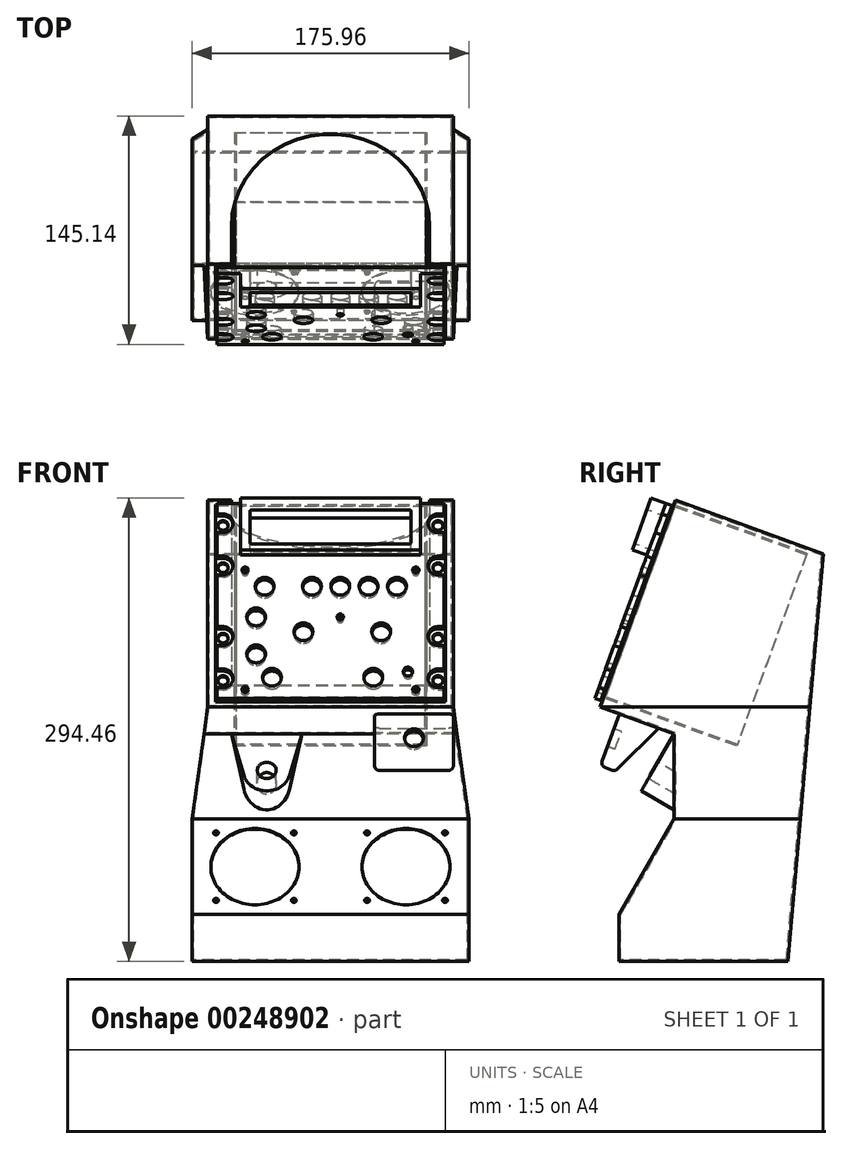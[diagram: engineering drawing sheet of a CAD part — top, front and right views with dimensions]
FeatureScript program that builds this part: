
annotation { "Feature Type Name" : "Feature", "Feature Type Description" : "" }
export const myFeature = defineFeature(function(context is Context, id is Id, definition is map)
    precondition{}
    {
        {
            var Q0;
            Q0=qCreatedBy(makeId("Right.planeOp"),FACE);
            var sketch = newSketch(context, id + "F0", { "sketchPlane" : qUnion([Q0])});
            skLineSegment(sketch, "E0", {"start": v(0, 0) * mm, "end": v(-47.88, -131.56) * mm});
            skLineSegment(sketch, "E1", {"start": v(-47.88, -131.56) * mm, "end": v(-0.9, -148.66) * mm});
            skLineSegment(sketch, "E2", {"start": v(-0.9, -148.66) * mm, "end": v(-0.9, -202.6) * mm});
            skLineSegment(sketch, "E3", {"start": v(-0.9, -202.6) * mm, "end": v(-35.9, -263.21) * mm});
            skLineSegment(sketch, "E4", {"start": v(-35.9, -263.21) * mm, "end": v(-35.9, -293.21) * mm});
            skLineSegment(sketch, "E5", {"start": v(-35.9, -293.21) * mm, "end": v(71.3, -293.21) * mm});
            skLineSegment(sketch, "E6", {"start": v(71.3, -293.21) * mm, "end": v(93.97, -34.2) * mm});
            skLineSegment(sketch, "E7", {"start": v(93.97, -34.2) * mm, "end": v(0, 0) * mm});
            skSolve(sketch);
        }
        {
            var Q0;
            Q0=qSketchRegion(id+"F0",true);
            extrude(context, id + "F1", {"entities" : qUnion([Q0]), "depth" : 200 * mm});
        }
        {
            var Q0;
            Q0=makeQuery(id+"F1.opExtrude","SWEPT_FACE",FACE,{"disambiguationData":[OSD([sQuery(id+"F0.wireOp",EDGE,"E2")])]});
            var sketch = newSketch(context, id + "F2", { "sketchPlane" : qUnion([Q0])});
            skLineSegment(sketch, "E8", {"start": v(178, 0) * mm, "end": v(178, -131.56) * mm});
            skLineSegment(sketch, "E9", {"start": v(178, -131.56) * mm, "end": v(187.98, -202.6) * mm});
            skLineSegment(sketch, "E10", {"start": v(187.98, -202.6) * mm, "end": v(187.98, -293.21) * mm});
            skLineSegment(sketch, "E11", {"start": v(187.98, -293.21) * mm, "end": v(228, -293.21) * mm});
            skLineSegment(sketch, "E12", {"start": v(228, -293.21) * mm, "end": v(228, 0) * mm});
            skLineSegment(sketch, "E13", {"start": v(228, 0) * mm, "end": v(178, 0) * mm});
            skLineSegment(sketch, "E14", {"start": v(0, 0) * mm, "end": v(22, 0) * mm});
            skLineSegment(sketch, "E15", {"start": v(22, 0) * mm, "end": v(22, -131.56) * mm});
            skLineSegment(sketch, "E16", {"start": v(22, -131.56) * mm, "end": v(12.02, -202.6) * mm});
            skLineSegment(sketch, "E17", {"start": v(12.02, -202.6) * mm, "end": v(12.02, -293.21) * mm});
            skLineSegment(sketch, "E18", {"start": v(12.02, -293.21) * mm, "end": v(-28, -293.21) * mm});
            skLineSegment(sketch, "E19", {"start": v(-28, -293.21) * mm, "end": v(-28, 0) * mm});
            skLineSegment(sketch, "E20", {"start": v(-28, 0) * mm, "end": v(22, 0) * mm});
            skLineSegment(sketch, "E21", {"start": v(22, -35.34) * mm, "end": v(0, -35.34) * mm, "construction": true});
            skLineSegment(sketch, "E22", {"start": v(178, -36.32) * mm, "end": v(200, -36.32) * mm, "construction": true});
            skSolve(sketch);
        }
        {
            var Q0;
            Q0=qSketchRegion(id+"F2",true);
            var Q1;
            Q1=makeQuery(id+"F1.opExtrude","SWEPT_FACE",FACE,{"disambiguationData":[OSD([sQuery(id+"F0.wireOp",EDGE,"E6")])]});
            extrude(context, id + "F3", {"entities" : qUnion([Q0]), "operationType" : NewBodyOperationType.REMOVE, "endBound" : BoundingType.UP_TO_SURFACE, "oppositeDirection" : true, "endBoundEntityFace" : qUnion([Q1]), "depth" : 25 * mm, "hasSecondDirection" : true, "secondDirectionOppositeDirection" : false, "secondDirectionDepth" : 150 * mm});
        }
        {
            var Q0;
            Q0=makeQuery(id+"F1.opExtrude","SWEPT_FACE",FACE,{"disambiguationData":[OSD([sQuery(id+"F0.wireOp",EDGE,"E0")])]});
            var sketch = newSketch(context, id + "F4", { "sketchPlane" : qUnion([Q0])});
            skLineSegment(sketch, "E23.bottom", {"start": v(37, -1) * mm, "end": v(163, -1) * mm});
            skLineSegment(sketch, "E23.top", {"start": v(37, -125) * mm, "end": v(163, -125) * mm});
            skLineSegment(sketch, "E23.left", {"start": v(37, -1) * mm, "end": v(37, -125) * mm});
            skLineSegment(sketch, "E23.right", {"start": v(163, -1) * mm, "end": v(163, -125) * mm});
            skSolve(sketch);
        }
        {
            var Q0;
            Q0=qSketchRegion(id+"F4",true);
            extrude(context, id + "F5", {"entities" : qUnion([Q0]), "operationType" : NewBodyOperationType.REMOVE, "oppositeDirection" : true, "depth" : 1 * mm});
        }
        {
            var Q0;
            Q0=makeQuery(id+"F5.boolean.opBoolean","COPY",FACE,{"derivedFrom":makeQuery(id+"F5.opExtrude","CAP_FACE",FACE,{"disambiguationData":[OSD([sQuery(id+"F4.wireOp",EDGE,"E23.bottom"),sQuery(id+"F4.wireOp",EDGE,"E23.top"),sQuery(id+"F4.wireOp",EDGE,"E23.left"),sQuery(id+"F4.wireOp",EDGE,"E23.right")])],"isStart":false})});
            shell(context, id + "F6", {"entities" : qUnion([Q0]), "thickness" : 1 * mm});
        }
        {
            var Q0;
            Q0=makeQuery(id+"F1.opExtrude","SWEPT_FACE",FACE,{"disambiguationData":[OSD([sQuery(id+"F0.wireOp",EDGE,"E7")])]});
            var sketch = newSketch(context, id + "F7", { "sketchPlane" : qUnion([Q0])});
            skLineSegment(sketch, "E24", {"start": v(37, 0) * mm, "end": v(37, 25) * mm});
            skLineSegment(sketch, "E25", {"start": v(163, 0) * mm, "end": v(163, 25) * mm});
            skArc(sketch, "E26", {"start": v(163, 25) * mm, "mid": v(100, 88) * mm, "end": v(37, 25) * mm});
            skLineSegment(sketch, "E27", {"start": v(37, 0) * mm, "end": v(163, 0) * mm});
            skSolve(sketch);
        }
        {
            var Q0;
            Q0=qSketchRegion(id+"F7",true);
            extrude(context, id + "F8", {"entities" : qUnion([Q0]), "operationType" : NewBodyOperationType.REMOVE, "endBound" : BoundingType.UP_TO_NEXT, "oppositeDirection" : true, "depth" : 25 * mm});
        }
        {
            var Q0;
            Q0=makeQuery(id+"F1.opExtrude","SWEPT_FACE",FACE,{"disambiguationData":[OSD([sQuery(id+"F0.wireOp",EDGE,"E3")])]});
            var sketch = newSketch(context, id + "F9", { "sketchPlane" : qUnion([Q0])});
            skCircle(sketch, "E28", {"center": v(52.02, -210.9) * mm, "radius": 28 * mm});
            skCircle(sketch, "E29", {"center": v(147.98, -210.9) * mm, "radius": 28 * mm});
            skLineSegment(sketch, "E30", {"start": v(52.02, -210.9) * mm, "end": v(52.02, -175.9) * mm, "construction": true});
            skLineSegment(sketch, "E31", {"start": v(52.02, -210.9) * mm, "end": v(52.02, -245.9) * mm, "construction": true});
            skSolve(sketch);
        }
        {
            var Q0;
            Q0=qSketchRegion(id+"F9",true);
            extrude(context, id + "F10", {"entities" : qUnion([Q0]), "operationType" : NewBodyOperationType.REMOVE, "endBound" : BoundingType.UP_TO_NEXT, "oppositeDirection" : true, "depth" : 25 * mm});
        }
        {
            var Q0;
            Q0=makeQuery(id+"F3.boolean.opBoolean","COPY",FACE,{"derivedFrom":makeQuery(id+"F3.opExtrude","SWEPT_FACE",FACE,{"disambiguationData":[OSD([sQuery(id+"F2.wireOp",EDGE,"E8")])]})});
            var sketch = newSketch(context, id + "F11", { "sketchPlane" : qUnion([Q0])});
            skLineSegment(sketch, "E32", {"start": v(-35.67, -136) * mm, "end": v(-47.64, -168.9) * mm});
            skLineSegment(sketch, "E33", {"start": v(-47.64, -168.9) * mm, "end": v(-38.24, -172.31) * mm});
            skLineSegment(sketch, "E34", {"start": v(-38.24, -172.31) * mm, "end": v(-10.93, -145) * mm});
            skLineSegment(sketch, "E35", {"start": v(-10.93, -145) * mm, "end": v(-35.67, -136) * mm});
            skSolve(sketch);
        }
        {
            var Q0;
            Q0=qSketchRegion(id+"F11",true);
            extrude(context, id + "F12", {"entities" : qUnion([Q0]), "operationType" : NewBodyOperationType.ADD, "oppositeDirection" : true, "depth" : 50 * mm});
        }
        {
            var Q0;
            Q0=makeQuery(id+"F12.opExtrude","CAP_EDGE",EDGE,{"disambiguationData":[OSD([sQuery(id+"F11.wireOp",EDGE,"E32")])],"isStart":false});
            var Q1;
            Q1=makeQuery(id+"F12.opExtrude","SWEPT_EDGE",EDGE,{"disambiguationData":[OSD([sQuery(id+"F11.wireOp",EDGE,"E32"),sQuery(id+"F11.wireOp",EDGE,"E33")])]});
            var Q2;
            Q2=makeQuery(id+"F12.opExtrude","CAP_EDGE",EDGE,{"disambiguationData":[OSD([sQuery(id+"F11.wireOp",EDGE,"E32")])],"isStart":true});
            var Q3;
            Q3=makeQuery(id+"F12.opExtrude","CAP_EDGE",EDGE,{"disambiguationData":[OSD([sQuery(id+"F11.wireOp",EDGE,"E34")])],"isStart":false});
            var Q4;
            Q4=makeQuery(id+"F12.opExtrude","SWEPT_EDGE",EDGE,{"disambiguationData":[OSD([sQuery(id+"F11.wireOp",EDGE,"E33"),sQuery(id+"F11.wireOp",EDGE,"E34")])]});
            var Q5;
            Q5=makeQuery(id+"F12.opExtrude","CAP_EDGE",EDGE,{"disambiguationData":[OSD([sQuery(id+"F11.wireOp",EDGE,"E34")])],"isStart":true});
            var Q6;
            Q6=makeQuery(id+"F12.opExtrude","CAP_EDGE",EDGE,{"disambiguationData":[OSD([sQuery(id+"F11.wireOp",EDGE,"E33")])],"isStart":true});
            var Q7;
            Q7=makeQuery(id+"F12.opExtrude","CAP_EDGE",EDGE,{"disambiguationData":[OSD([sQuery(id+"F11.wireOp",EDGE,"E33")])],"isStart":false});
            fillet(context, id + "F13", {"entities" : qUnion([Q0, Q1, Q2, Q3, Q4, Q5, Q6, Q7]), "radius" : 3 * mm, "tangentPropagation" : true, "allowEdgeOverflow" : false});
        }
        {
            var Q0;
            Q0=makeQuery(id+"F1.opExtrude","SWEPT_EDGE",EDGE,{"disambiguationData":[OSD([sQuery(id+"F0.wireOp",EDGE,"E1"),sQuery(id+"F0.wireOp",EDGE,"E2")])]});
            cPlane(context, id + "F14", {"entities" : qUnion([Q0]), "cplaneType" : CPlaneType.LINE_ANGLE, "offset" : 25 * mm, "angle" : 30 * degree, "width" : 150 * mm, "height" : 150 * mm});
        }
        {
            var Q0;
            Q0=qCreatedBy(id+"F14.planeOp",FACE);
            var sketch = newSketch(context, id + "F15", { "sketchPlane" : qUnion([Q0])});
            skLineSegment(sketch, "E36", {"start": v(37, -129.2) * mm, "end": v(44.99, -159.7) * mm});
            skLineSegment(sketch, "E37", {"start": v(82, -129.2) * mm, "end": v(74.01, -159.7) * mm});
            skArc(sketch, "E38", {"start": v(44.99, -159.7) * mm, "mid": v(59.5, -170.9) * mm, "end": v(74.01, -159.7) * mm});
            skLineSegment(sketch, "E39", {"start": v(37, -129.2) * mm, "end": v(82, -129.2) * mm});
            skSolve(sketch);
        }
        {
            var Q0;
            Q0=qSketchRegion(id+"F15",true);
            var Q1;
            Q1=makeQuery(id+"F1.opExtrude","SWEPT_FACE",FACE,{"disambiguationData":[OSD([sQuery(id+"F0.wireOp",EDGE,"E2")])]});
            extrude(context, id + "F16", {"entities" : qUnion([Q0]), "operationType" : NewBodyOperationType.ADD, "endBound" : BoundingType.UP_TO_SURFACE, "oppositeDirection" : true, "endBoundEntityFace" : qUnion([Q1]), "depth" : 25 * mm});
        }
        {
            var Q0;
            Q0=makeQuery(id+"F16.opExtrude","CAP_FACE",FACE,{"disambiguationData":[OSD([sQuery(id+"F15.wireOp",EDGE,"E36"),sQuery(id+"F15.wireOp",EDGE,"E37"),sQuery(id+"F15.wireOp",EDGE,"E38"),sQuery(id+"F15.wireOp",EDGE,"E39")])],"isStart":true});
            var sketch = newSketch(context, id + "F17", { "sketchPlane" : qUnion([Q0])});
            skCircle(sketch, "E40", {"center": v(59.5, -155.9) * mm, "radius": 6 * mm});
            skSolve(sketch);
        }
        {
            var Q0;
            Q0=qSketchRegion(id+"F17",true);
            extrude(context, id + "F18", {"entities" : qUnion([Q0]), "operationType" : NewBodyOperationType.REMOVE, "endBound" : BoundingType.UP_TO_NEXT, "oppositeDirection" : true, "depth" : 25 * mm});
        }
        {
            var Q0;
            Q0=makeQuery(id+"F12.opExtrude","SWEPT_FACE",FACE,{"disambiguationData":[OSD([sQuery(id+"F11.wireOp",EDGE,"E32")])]});
            var sketch = newSketch(context, id + "F19", { "sketchPlane" : qUnion([Q0])});
            skCircle(sketch, "E41", {"center": v(153, -156) * mm, "radius": 6 * mm});
            skLineSegment(sketch, "E42", {"start": v(153, -156) * mm, "end": v(153, -140) * mm, "construction": true});
            skLineSegment(sketch, "E43", {"start": v(153, -156) * mm, "end": v(153, -172) * mm, "construction": true});
            skLineSegment(sketch, "E44", {"start": v(153, -156) * mm, "end": v(131, -156) * mm, "construction": true});
            skLineSegment(sketch, "E45", {"start": v(153, -156) * mm, "end": v(175, -156) * mm, "construction": true});
            skSolve(sketch);
        }
        {
            var Q0;
            Q0=qSketchRegion(id+"F19",true);
            extrude(context, id + "F20", {"entities" : qUnion([Q0]), "operationType" : NewBodyOperationType.REMOVE, "oppositeDirection" : true, "depth" : 5 * mm});
        }
        {
            var Q0;
            Q0=makeQuery(id+"F1.opExtrude","SWEPT_FACE",FACE,{"disambiguationData":[OSD([sQuery(id+"F0.wireOp",EDGE,"E0")])]});
            var sketch = newSketch(context, id + "F21", { "sketchPlane" : qUnion([Q0])});
            skLineSegment(sketch, "E46.bottom", {"start": v(27, -3.33) * mm, "end": v(173, -3.33) * mm});
            skLineSegment(sketch, "E46.top", {"start": v(27, -136.68) * mm, "end": v(173, -136.68) * mm});
            skLineSegment(sketch, "E46.left", {"start": v(27, -3.33) * mm, "end": v(27, -136.68) * mm});
            skLineSegment(sketch, "E46.right", {"start": v(173, -3.33) * mm, "end": v(173, -136.68) * mm});
            skLineSegment(sketch, "E47", {"start": v(27, -136.68) * mm, "end": v(22, -136.68) * mm, "construction": true});
            skLineSegment(sketch, "E48", {"start": v(173, -136.68) * mm, "end": v(178, -136.68) * mm, "construction": true});
            skLineSegment(sketch, "E49", {"start": v(27, -136.68) * mm, "end": v(27, -140) * mm, "construction": true});
            skLineSegment(sketch, "E50", {"start": v(27, -3.33) * mm, "end": v(27, 0) * mm, "construction": true});
            skSolve(sketch);
        }
        {
            var Q0;
            Q0=qSketchRegion(id+"F21",true);
            extrude(context, id + "F22", {"entities" : qUnion([Q0]), "depth" : 1 * mm});
        }
        {
            var Q0;
            Q0=makeQuery(id+"F22.opExtrude","CAP_FACE",FACE,{"disambiguationData":[OSD([sQuery(id+"F21.wireOp",EDGE,"E46.bottom"),sQuery(id+"F21.wireOp",EDGE,"E46.top"),sQuery(id+"F21.wireOp",EDGE,"E46.left"),sQuery(id+"F21.wireOp",EDGE,"E46.right")])],"isStart":false});
            var sketch = newSketch(context, id + "F23", { "sketchPlane" : qUnion([Q0])});
            skLineSegment(sketch, "E51.bottom", {"start": v(27.8, -4.13) * mm, "end": v(172.2, -4.13) * mm});
            skLineSegment(sketch, "E51.top", {"start": v(27.8, -135.88) * mm, "end": v(172.2, -135.88) * mm});
            skLineSegment(sketch, "E51.left", {"start": v(27.8, -4.13) * mm, "end": v(27.8, -11.26) * mm});
            skLineSegment(sketch, "E51.right", {"start": v(172.2, -4.13) * mm, "end": v(172.2, -11.26) * mm});
            skArc(sketch, "E52", {"start": v(168.24, -11.26) * mm, "mid": v(161.89, -17.61) * mm, "end": v(168.24, -23.96) * mm});
            skArc(sketch, "E53", {"start": v(168.24, -39.84) * mm, "mid": v(161.89, -46.19) * mm, "end": v(168.24, -52.54) * mm});
            skArc(sketch, "E54", {"start": v(168.24, -87.46) * mm, "mid": v(161.89, -93.81) * mm, "end": v(168.24, -100.16) * mm});
            skArc(sketch, "E55", {"start": v(168.24, -116.04) * mm, "mid": v(161.89, -122.39) * mm, "end": v(168.24, -128.74) * mm});
            skArc(sketch, "E56", {"start": v(31.76, -23.96) * mm, "mid": v(38.11, -17.61) * mm, "end": v(31.76, -11.26) * mm});
            skArc(sketch, "E57", {"start": v(31.76, -52.54) * mm, "mid": v(38.11, -46.19) * mm, "end": v(31.76, -39.84) * mm});
            skArc(sketch, "E58", {"start": v(31.76, -100.16) * mm, "mid": v(38.11, -93.81) * mm, "end": v(31.76, -87.46) * mm});
            skArc(sketch, "E59", {"start": v(31.76, -128.74) * mm, "mid": v(38.11, -122.39) * mm, "end": v(31.76, -116.04) * mm});
            skLineSegment(sketch, "E60", {"start": v(31.76, -11.26) * mm, "end": v(27.8, -11.26) * mm});
            skLineSegment(sketch, "E61", {"start": v(31.76, -23.96) * mm, "end": v(27.8, -23.96) * mm});
            skLineSegment(sketch, "E62", {"start": v(31.76, -39.84) * mm, "end": v(27.8, -39.84) * mm});
            skLineSegment(sketch, "E63", {"start": v(31.76, -52.54) * mm, "end": v(27.8, -52.54) * mm});
            skLineSegment(sketch, "E64", {"start": v(168.24, -11.26) * mm, "end": v(172.2, -11.26) * mm});
            skLineSegment(sketch, "E65", {"start": v(168.24, -23.96) * mm, "end": v(172.2, -23.96) * mm});
            skLineSegment(sketch, "E66", {"start": v(168.24, -39.84) * mm, "end": v(172.2, -39.84) * mm});
            skLineSegment(sketch, "E67", {"start": v(168.24, -52.54) * mm, "end": v(172.2, -52.54) * mm});
            skLineSegment(sketch, "E68", {"start": v(31.76, -87.46) * mm, "end": v(27.8, -87.46) * mm});
            skLineSegment(sketch, "E69", {"start": v(31.76, -100.16) * mm, "end": v(27.8, -100.16) * mm});
            skLineSegment(sketch, "E70", {"start": v(31.76, -116.04) * mm, "end": v(27.8, -116.04) * mm});
            skLineSegment(sketch, "E71", {"start": v(31.76, -128.74) * mm, "end": v(27.8, -128.74) * mm});
            skLineSegment(sketch, "E72", {"start": v(168.24, -87.46) * mm, "end": v(172.2, -87.46) * mm});
            skLineSegment(sketch, "E73", {"start": v(168.24, -100.16) * mm, "end": v(172.2, -100.16) * mm});
            skLineSegment(sketch, "E74", {"start": v(168.24, -116.04) * mm, "end": v(172.2, -116.04) * mm});
            skLineSegment(sketch, "E75", {"start": v(168.24, -128.74) * mm, "end": v(172.2, -128.74) * mm});
            skLineSegment(sketch, "E76.trimOffspring", {"start": v(27.8, -23.96) * mm, "end": v(27.8, -39.84) * mm});
            skLineSegment(sketch, "E77.trimOffspring", {"start": v(27.8, -52.54) * mm, "end": v(27.8, -87.46) * mm});
            skLineSegment(sketch, "E78.trimOffspring", {"start": v(27.8, -100.16) * mm, "end": v(27.8, -116.04) * mm});
            skLineSegment(sketch, "E79.trimOffspring", {"start": v(27.8, -128.74) * mm, "end": v(27.8, -135.88) * mm});
            skLineSegment(sketch, "E80.trimOffspring", {"start": v(172.2, -23.96) * mm, "end": v(172.2, -39.84) * mm});
            skLineSegment(sketch, "E81.trimOffspring", {"start": v(172.2, -52.54) * mm, "end": v(172.2, -87.46) * mm});
            skLineSegment(sketch, "E82.trimOffspring", {"start": v(172.2, -100.16) * mm, "end": v(172.2, -116.04) * mm});
            skLineSegment(sketch, "E83.trimOffspring", {"start": v(172.2, -128.74) * mm, "end": v(172.2, -135.88) * mm});
            skSolve(sketch);
        }
        {
            var Q0;
            Q0=qSketchRegion(id+"F23",true);
            extrude(context, id + "F24", {"entities" : qUnion([Q0]), "operationType" : NewBodyOperationType.ADD, "depth" : 4 * mm});
        }
        {
            var Q0;
            Q0=makeQuery(id+"F22.opExtrude","CAP_FACE",FACE,{"disambiguationData":[OSD([sQuery(id+"F21.wireOp",EDGE,"E46.bottom"),sQuery(id+"F21.wireOp",EDGE,"E46.top"),sQuery(id+"F21.wireOp",EDGE,"E46.left"),sQuery(id+"F21.wireOp",EDGE,"E46.right")])],"isStart":false});
            var sketch = newSketch(context, id + "F25", { "sketchPlane" : qUnion([Q0])});
            skCircle(sketch, "E84", {"center": v(31.76, -17.61) * mm, "radius": 3.24 * mm});
            skCircle(sketch, "E85", {"center": v(168.24, -17.61) * mm, "radius": 3.24 * mm});
            skCircle(sketch, "E86", {"center": v(168.24, -46.19) * mm, "radius": 3.24 * mm});
            skCircle(sketch, "E87", {"center": v(31.76, -46.19) * mm, "radius": 3.24 * mm});
            skCircle(sketch, "E88", {"center": v(31.76, -93.81) * mm, "radius": 3.24 * mm});
            skCircle(sketch, "E89", {"center": v(31.76, -122.39) * mm, "radius": 3.24 * mm});
            skCircle(sketch, "E90", {"center": v(168.24, -93.81) * mm, "radius": 3.24 * mm});
            skCircle(sketch, "E91", {"center": v(168.24, -122.39) * mm, "radius": 3.24 * mm});
            skSolve(sketch);
        }
        {
            var Q0;
            Q0=qSketchRegion(id+"F25",true);
            var Q1;
            Q1=makeQuery(id+"F6.opShell","OFFSET_FACE",FACE,{"disambiguationData":[OSD([sQuery(id+"F0.wireOp",EDGE,"E0"),sQuery(id+"F4.wireOp",EDGE,"E23.bottom"),sQuery(id+"F4.wireOp",EDGE,"E23.top"),sQuery(id+"F4.wireOp",EDGE,"E23.left"),sQuery(id+"F4.wireOp",EDGE,"E23.right")])]});
            extrude(context, id + "F26", {"entities" : qUnion([Q0]), "operationType" : NewBodyOperationType.REMOVE, "endBound" : BoundingType.UP_TO_SURFACE, "oppositeDirection" : true, "endBoundEntityFace" : qUnion([Q1]), "depth" : 25 * mm});
        }
        {
            var Q0;
            Q0=makeQuery(id+"F22.opExtrude","CAP_FACE",FACE,{"disambiguationData":[OSD([sQuery(id+"F21.wireOp",EDGE,"E46.bottom"),sQuery(id+"F21.wireOp",EDGE,"E46.top"),sQuery(id+"F21.wireOp",EDGE,"E46.left"),sQuery(id+"F21.wireOp",EDGE,"E46.right")])],"isStart":true});
            var sketch = newSketch(context, id + "F27", { "sketchPlane" : qUnion([Q0])});
            skLineSegment(sketch, "E92.bottom", {"start": v(-161, -3.33) * mm, "end": v(-39, -3.33) * mm});
            skLineSegment(sketch, "E92.top", {"start": v(-161, -133.68) * mm, "end": v(-39, -133.68) * mm});
            skLineSegment(sketch, "E92.left", {"start": v(-161, -3.33) * mm, "end": v(-161, -133.68) * mm});
            skLineSegment(sketch, "E92.right", {"start": v(-39, -3.33) * mm, "end": v(-39, -133.67) * mm});
            skLineSegment(sketch, "E93.bottom", {"start": v(-160, -4.33) * mm, "end": v(-40, -4.33) * mm});
            skLineSegment(sketch, "E93.top", {"start": v(-160, -132.68) * mm, "end": v(-40, -132.68) * mm});
            skLineSegment(sketch, "E93.left", {"start": v(-160, -4.33) * mm, "end": v(-160, -132.68) * mm});
            skLineSegment(sketch, "E93.right", {"start": v(-40, -4.33) * mm, "end": v(-40, -132.68) * mm});
            skSolve(sketch);
        }
        {
            var Q0;
            Q0=qSketchRegion(id+"F27",true);
            extrude(context, id + "F28", {"entities" : qUnion([Q0]), "operationType" : NewBodyOperationType.ADD, "depth" : 90 * mm});
        }
        {
            var Q0;
            Q0=makeQuery(id+"F24.opExtrude","CAP_FACE",FACE,{"disambiguationData":[OSD([sQuery(id+"F23.wireOp",EDGE,"E51.bottom"),sQuery(id+"F23.wireOp",EDGE,"E51.top"),sQuery(id+"F23.wireOp",EDGE,"E51.left"),sQuery(id+"F23.wireOp",EDGE,"E51.right"),sQuery(id+"F23.wireOp",EDGE,"E52"),sQuery(id+"F23.wireOp",EDGE,"E53"),sQuery(id+"F23.wireOp",EDGE,"E54"),sQuery(id+"F23.wireOp",EDGE,"E55"),sQuery(id+"F23.wireOp",EDGE,"E56"),sQuery(id+"F23.wireOp",EDGE,"E57"),sQuery(id+"F23.wireOp",EDGE,"E58"),sQuery(id+"F23.wireOp",EDGE,"E59"),sQuery(id+"F23.wireOp",EDGE,"E60"),sQuery(id+"F23.wireOp",EDGE,"E61"),sQuery(id+"F23.wireOp",EDGE,"E62"),sQuery(id+"F23.wireOp",EDGE,"E63"),sQuery(id+"F23.wireOp",EDGE,"E64"),sQuery(id+"F23.wireOp",EDGE,"E65"),sQuery(id+"F23.wireOp",EDGE,"E66"),sQuery(id+"F23.wireOp",EDGE,"E67"),sQuery(id+"F23.wireOp",EDGE,"E68"),sQuery(id+"F23.wireOp",EDGE,"E69"),sQuery(id+"F23.wireOp",EDGE,"E70"),sQuery(id+"F23.wireOp",EDGE,"E71"),sQuery(id+"F23.wireOp",EDGE,"E72"),sQuery(id+"F23.wireOp",EDGE,"E73"),sQuery(id+"F23.wireOp",EDGE,"E74"),sQuery(id+"F23.wireOp",EDGE,"E75"),sQuery(id+"F23.wireOp",EDGE,"E76.trimOffspring"),sQuery(id+"F23.wireOp",EDGE,"E77.trimOffspring"),sQuery(id+"F23.wireOp",EDGE,"E78.trimOffspring"),sQuery(id+"F23.wireOp",EDGE,"E79.trimOffspring"),sQuery(id+"F23.wireOp",EDGE,"E80.trimOffspring"),sQuery(id+"F23.wireOp",EDGE,"E81.trimOffspring"),sQuery(id+"F23.wireOp",EDGE,"E82.trimOffspring"),sQuery(id+"F23.wireOp",EDGE,"E83.trimOffspring")])],"isStart":false});
            var sketch = newSketch(context, id + "F29", { "sketchPlane" : qUnion([Q0])});
            skCircle(sketch, "E94", {"center": v(154.2, -49.13) * mm, "radius": 2 * mm});
            skCircle(sketch, "E95", {"center": v(45.8, -49.13) * mm, "radius": 2 * mm});
            skCircle(sketch, "E96", {"center": v(45.8, -129.88) * mm, "radius": 2 * mm});
            skCircle(sketch, "E97", {"center": v(154.2, -129.88) * mm, "radius": 2 * mm});
            skCircle(sketch, "E98", {"center": v(142.2, -60.13) * mm, "radius": 6 * mm});
            skCircle(sketch, "E99.1.0.0", {"center": v(124.2, -60.12) * mm, "radius": 6 * mm});
            skCircle(sketch, "E99.2.0.0", {"center": v(106.2, -60.13) * mm, "radius": 6 * mm});
            skCircle(sketch, "E99.3.0.0", {"center": v(88.2, -60.13) * mm, "radius": 6 * mm});
            skLineSegment(sketch, "E99.direction1", {"start": v(142.2, -60.13) * mm, "end": v(124.2, -60.13) * mm, "construction": true});
            skCircle(sketch, "E100", {"center": v(58.2, -60.13) * mm, "radius": 6 * mm});
            skCircle(sketch, "E101", {"center": v(132.2, -90.88) * mm, "radius": 6 * mm});
            skCircle(sketch, "E102", {"center": v(82.8, -90.88) * mm, "radius": 6 * mm});
            skCircle(sketch, "E103", {"center": v(52.8, -80.88) * mm, "radius": 6 * mm});
            skCircle(sketch, "E104", {"center": v(52.8, -105.88) * mm, "radius": 6 * mm});
            skCircle(sketch, "E105", {"center": v(62.8, -121.68) * mm, "radius": 6 * mm});
            skCircle(sketch, "E106", {"center": v(127.2, -121.68) * mm, "radius": 6 * mm});
            skCircle(sketch, "E107", {"center": v(149.2, -117.88) * mm, "radius": 3 * mm});
            skCircle(sketch, "E108", {"center": v(106.2, -80.88) * mm, "radius": 2 * mm});
            skSolve(sketch);
        }
        {
            var Q0;
            Q0=qSketchRegion(id+"F29",true);
            extrude(context, id + "F30", {"entities" : qUnion([Q0]), "operationType" : NewBodyOperationType.REMOVE, "endBound" : BoundingType.UP_TO_NEXT, "oppositeDirection" : true, "depth" : 25 * mm});
        }
        {
            var Q0;
            Q0=makeQuery(id+"F1.opExtrude","SWEPT_FACE",FACE,{"disambiguationData":[OSD([sQuery(id+"F0.wireOp",EDGE,"E3")])]});
            var sketch = newSketch(context, id + "F31", { "sketchPlane" : qUnion([Q0])});
            skLineSegment(sketch, "E109", {"start": v(52.02, -210.9) * mm, "end": v(76.77, -186.15) * mm, "construction": true});
            skCircle(sketch, "E110", {"center": v(76.77, -186.15) * mm, "radius": 1.5 * mm});
            skLineSegment(sketch, "E111", {"start": v(52.02, -210.9) * mm, "end": v(27.27, -235.65) * mm, "construction": true});
            skCircle(sketch, "E112", {"center": v(27.27, -235.65) * mm, "radius": 1.5 * mm});
            skCircle(sketch, "E113", {"center": v(76.77, -235.65) * mm, "radius": 1.5 * mm});
            skCircle(sketch, "E114", {"center": v(27.27, -186.15) * mm, "radius": 1.5 * mm});
            skLineSegment(sketch, "E115", {"start": v(147.98, -210.9) * mm, "end": v(123.23, -186.15) * mm, "construction": true});
            skCircle(sketch, "E116", {"center": v(123.23, -186.15) * mm, "radius": 1.5 * mm});
            skCircle(sketch, "E117", {"center": v(123.23, -235.65) * mm, "radius": 1.5 * mm});
            skLineSegment(sketch, "E118", {"start": v(147.98, -210.9) * mm, "end": v(172.73, -235.65) * mm, "construction": true});
            skCircle(sketch, "E119", {"center": v(172.73, -235.65) * mm, "radius": 1.5 * mm});
            skCircle(sketch, "E120", {"center": v(172.73, -186.15) * mm, "radius": 1.5 * mm});
            skSolve(sketch);
        }
        {
            var Q0;
            Q0=qSketchRegion(id+"F31",true);
            extrude(context, id + "F32", {"entities" : qUnion([Q0]), "operationType" : NewBodyOperationType.REMOVE, "endBound" : BoundingType.UP_TO_NEXT, "oppositeDirection" : true, "depth" : 25 * mm});
        }
        {
            var Q0;
            Q0=makeQuery(id+"F24.opExtrude","CAP_FACE",FACE,{"disambiguationData":[OSD([sQuery(id+"F23.wireOp",EDGE,"E51.bottom"),sQuery(id+"F23.wireOp",EDGE,"E51.top"),sQuery(id+"F23.wireOp",EDGE,"E51.left"),sQuery(id+"F23.wireOp",EDGE,"E51.right"),sQuery(id+"F23.wireOp",EDGE,"E52"),sQuery(id+"F23.wireOp",EDGE,"E53"),sQuery(id+"F23.wireOp",EDGE,"E54"),sQuery(id+"F23.wireOp",EDGE,"E55"),sQuery(id+"F23.wireOp",EDGE,"E56"),sQuery(id+"F23.wireOp",EDGE,"E57"),sQuery(id+"F23.wireOp",EDGE,"E58"),sQuery(id+"F23.wireOp",EDGE,"E59"),sQuery(id+"F23.wireOp",EDGE,"E60"),sQuery(id+"F23.wireOp",EDGE,"E61"),sQuery(id+"F23.wireOp",EDGE,"E62"),sQuery(id+"F23.wireOp",EDGE,"E63"),sQuery(id+"F23.wireOp",EDGE,"E64"),sQuery(id+"F23.wireOp",EDGE,"E65"),sQuery(id+"F23.wireOp",EDGE,"E66"),sQuery(id+"F23.wireOp",EDGE,"E67"),sQuery(id+"F23.wireOp",EDGE,"E68"),sQuery(id+"F23.wireOp",EDGE,"E69"),sQuery(id+"F23.wireOp",EDGE,"E70"),sQuery(id+"F23.wireOp",EDGE,"E71"),sQuery(id+"F23.wireOp",EDGE,"E72"),sQuery(id+"F23.wireOp",EDGE,"E73"),sQuery(id+"F23.wireOp",EDGE,"E74"),sQuery(id+"F23.wireOp",EDGE,"E75"),sQuery(id+"F23.wireOp",EDGE,"E76.trimOffspring"),sQuery(id+"F23.wireOp",EDGE,"E77.trimOffspring"),sQuery(id+"F23.wireOp",EDGE,"E78.trimOffspring"),sQuery(id+"F23.wireOp",EDGE,"E79.trimOffspring"),sQuery(id+"F23.wireOp",EDGE,"E80.trimOffspring"),sQuery(id+"F23.wireOp",EDGE,"E81.trimOffspring"),sQuery(id+"F23.wireOp",EDGE,"E82.trimOffspring"),sQuery(id+"F23.wireOp",EDGE,"E83.trimOffspring")])],"isStart":false});
            var sketch = newSketch(context, id + "F33", { "sketchPlane" : qUnion([Q0])});
            skLineSegment(sketch, "E121.bottom", {"start": v(42.8, -4.13) * mm, "end": v(157.2, -4.13) * mm});
            skLineSegment(sketch, "E121.top", {"start": v(42.8, -39.13) * mm, "end": v(157.2, -39.13) * mm});
            skLineSegment(sketch, "E121.left", {"start": v(42.8, -4.13) * mm, "end": v(42.8, -39.13) * mm});
            skLineSegment(sketch, "E121.right", {"start": v(157.2, -4.13) * mm, "end": v(157.2, -39.13) * mm});
            skSolve(sketch);
        }
        {
            var Q0;
            Q0=qSketchRegion(id+"F33",true);
            extrude(context, id + "F34", {"entities" : qUnion([Q0]), "operationType" : NewBodyOperationType.ADD, "depth" : 10 * mm});
        }
        {
            var Q0;
            Q0=makeQuery(id+"F34.opExtrude","CAP_FACE",FACE,{"disambiguationData":[OSD([sQuery(id+"F33.wireOp",EDGE,"E121.bottom"),sQuery(id+"F33.wireOp",EDGE,"E121.top"),sQuery(id+"F33.wireOp",EDGE,"E121.left"),sQuery(id+"F33.wireOp",EDGE,"E121.right")])],"isStart":false});
            var sketch = newSketch(context, id + "F35", { "sketchPlane" : qUnion([Q0])});
            skLineSegment(sketch, "E122.bottom", {"start": v(49.8, -12.13) * mm, "end": v(150.2, -12.13) * mm});
            skLineSegment(sketch, "E122.top", {"start": v(49.8, -35.13) * mm, "end": v(150.2, -35.13) * mm});
            skLineSegment(sketch, "E122.left", {"start": v(48.8, -13.13) * mm, "end": v(48.8, -34.13) * mm});
            skLineSegment(sketch, "E122.right", {"start": v(151.2, -13.13) * mm, "end": v(151.2, -34.13) * mm});
            skPoint(sketch, "E123.visualSharp", {"position": v(48.8, -12.13) * mm});
            skArc(sketch, "E123.filletArc", {"start": v(49.8, -12.13) * mm, "mid": v(49.1, -12.42) * mm, "end": v(48.8, -13.13) * mm});
            skPoint(sketch, "E124.visualSharp", {"position": v(151.2, -12.13) * mm});
            skArc(sketch, "E124.filletArc", {"start": v(151.2, -13.13) * mm, "mid": v(150.9, -12.42) * mm, "end": v(150.2, -12.13) * mm});
            skPoint(sketch, "E125.visualSharp", {"position": v(151.2, -35.13) * mm});
            skArc(sketch, "E125.filletArc", {"start": v(150.2, -35.13) * mm, "mid": v(150.9, -34.83) * mm, "end": v(151.2, -34.13) * mm});
            skPoint(sketch, "E126.visualSharp", {"position": v(48.8, -35.13) * mm});
            skArc(sketch, "E126.filletArc", {"start": v(48.8, -34.13) * mm, "mid": v(49.1, -34.83) * mm, "end": v(49.8, -35.13) * mm});
            skSolve(sketch);
        }
        {
            var Q0;
            Q0=qSketchRegion(id+"F35",true);
            extrude(context, id + "F36", {"entities" : qUnion([Q0]), "operationType" : NewBodyOperationType.REMOVE, "endBound" : BoundingType.UP_TO_NEXT, "oppositeDirection" : true, "depth" : 25 * mm});
        }
    });
